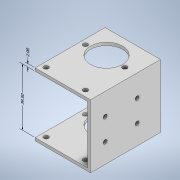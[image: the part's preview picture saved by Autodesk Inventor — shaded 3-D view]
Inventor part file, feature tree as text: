
AUTODESK INVENTOR PART (.ipt)
format: ipt  version: 2022 (Build 260153000, 153)  size: 173,056 bytes
history: native  units: mm
features: sketch x5, other x3, hole x3, extrude x2
ambient origin geometry x8: Origin, YZ Plane, XZ Plane, XY Plane, X Axis, Y Axis, Z Axis, Center Point
bodies: Body1 (feature_tree)
feature tree (13):
  other  "ソリッド1"
  extrude  "押し出し1"  Depth=48.0mm
  extrude  "押し出し2"  Depth=38.0mm
  hole  "穴1"  [1 undecoded]
  hole  "穴2"  [1 undecoded]
  hole  "穴4"  [1 undecoded]
  sketch  "スケッチ1"
  sketch  "スケッチ2"
  sketch  "スケッチ3"
  sketch  "スケッチ4"
  sketch  "スケッチ6"
  other  "長さ寸法 1"
  other  "長さ寸法 2"
note: 3 required parameter values undecoded (feature->parameter linkage not recoverable at this tier; creation-order binding heuristic only, values carry confidence <= 0.55)
